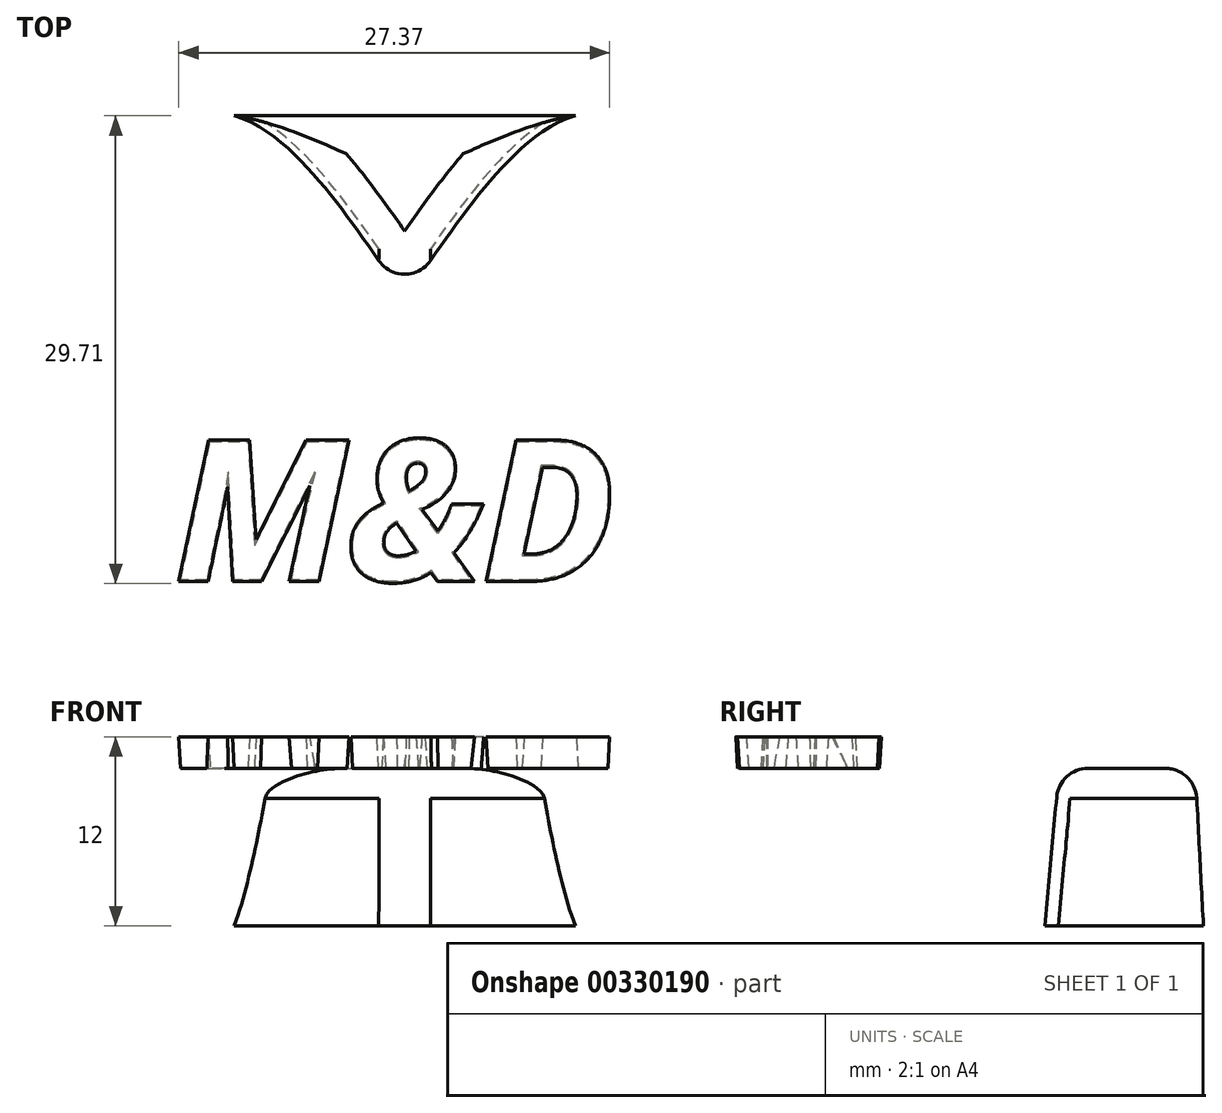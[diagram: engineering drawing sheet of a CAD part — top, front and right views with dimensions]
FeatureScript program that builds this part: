
annotation { "Feature Type Name" : "Feature", "Feature Type Description" : "" }
export const myFeature = defineFeature(function(context is Context, id is Id, definition is map)
    precondition{}
    {
        {
            var Q0;
            Q0=qCreatedBy(makeId("Top.planeOp"),FACE);
            var sketch = newSketch(context, id + "F0", { "sketchPlane" : qUnion([Q0])});
            skLineSegment(sketch, "E0.bottom", {"start": v(-22.5, 22.5) * mm, "end": v(22.5, 22.5) * mm});
            skLineSegment(sketch, "E0.top", {"start": v(-22.5, -22.5) * mm, "end": v(22.5, -22.5) * mm});
            skLineSegment(sketch, "E0.left", {"start": v(-22.5, 22.5) * mm, "end": v(-22.5, -22.5) * mm});
            skLineSegment(sketch, "E0.right", {"start": v(22.5, 22.5) * mm, "end": v(22.5, -22.5) * mm});
            skPoint(sketch, "E0.middle", {"position": v(0, 0) * mm});
            skPoint(sketch, "E1.0.internal.snap0", {"position": v(0, -22.5) * mm});
            skFitSpline(sketch, "E1", {"points": [v(0, -20.95) * mm, v(-22.5, 0) * mm, v(-13.19, 22.5) * mm, v(0, 10.86) * mm], "startDerivative": vector(-82.78, 43.98) * mm, "endDerivative": vector(45.64, -67.78) * mm});
            skFitSpline(sketch, "E2.MirrorCS", {"points": [v(0, -20.95) * mm, v(22.5, 0) * mm, v(13.19, 22.5) * mm, v(0, 10.86) * mm], "startDerivative": vector(82.78, 43.98) * mm, "endDerivative": vector(-45.64, -67.78) * mm});
            skSolve(sketch);
        }
        {
            var Q0;
            {var subQ4=sQuery(id+"F0.wireOp",EDGE,"E1");var subQ6=sQuery(id+"F0.wireOp",EDGE,"E0.bottom");var subQ12=makeQuery(id+"F0.imprint","INTERSECT",VERTEX,{"disambiguationData":[OD(0.0)],"derivedFrom":[subQ6,subQ4]});Q0=makeQuery(id+"F0.imprint","IMPRINT",FACE,{"disambiguationData":[TD([[makeQuery(id+"F0.imprint","IMPRINT",EDGE,{"disambiguationData":[TD([[subQ12,-1.0]])],"derivedFrom":subQ6}),-1.0]])]});}
            extrude(context, id + "F1", {"entities" : qUnion([Q0]), "depth" : 10 * mm, "hasDraft" : true, "draftAngle" : 3 * degree, "draftPullDirection" : true});
        }
        {
            var Q0;
            Q0=makeQuery(id+"F1.opExtrude","CAP_FACE",FACE,{"disambiguationData":[OSD([sQuery(id+"F0.wireOp",EDGE,"E0.bottom"),sQuery(id+"F0.wireOp",EDGE,"E0.left"),sQuery(id+"F0.wireOp",EDGE,"E0.right"),sQuery(id+"F0.wireOp",EDGE,"E1"),sQuery(id+"F0.wireOp",EDGE,"E2.MirrorCS")])],"isStart":false});
            var Q1;
            {var subQ0=sQuery(id+"F0.wireOp",EDGE,"E2.MirrorCS");var subQ1=sQuery(id+"F0.wireOp",EDGE,"E1");Q1=makeQuery(id+"F1.opExtrude","SWEPT_EDGE",EDGE,{"disambiguationData":[OSD([subQ1,subQ0]),TDD([makeQuery(id+"F0.imprint","INTERSECT",VERTEX,{"disambiguationData":[OD(0.0)],"derivedFrom":[subQ1,subQ0]})])]});}
            fillet(context, id + "F2", {"entities" : qUnion([Q0, Q1]), "radius" : 2 * mm, "tangentPropagation" : true, "allowEdgeOverflow" : false});
        }
        {
            var Q0;
            Q0=makeQuery(id+"F1.opExtrude","CAP_FACE",FACE,{"disambiguationData":[OSD([sQuery(id+"F0.wireOp",EDGE,"E0.bottom"),sQuery(id+"F0.wireOp",EDGE,"E0.left"),sQuery(id+"F0.wireOp",EDGE,"E0.right"),sQuery(id+"F0.wireOp",EDGE,"E1"),sQuery(id+"F0.wireOp",EDGE,"E2.MirrorCS")])],"isStart":false});
            var sketch = newSketch(context, id + "F3", { "sketchPlane" : qUnion([Q0])});
            skText(sketch, "E3", { "text": "M&D", "fontName": "OpenSans-BoldItalic.ttf"});
            const initialGuessF3  = {"E3": [-0.01454, -0.00698, 1, 0, 0.00885]};
            skSetInitialGuess(sketch, initialGuessF3);
            skSolve(sketch);
        }
        {
            var Q0;
            Q0 = qSketchRegion(id + "F3", true);
            extrude(context, id + "F4", {"entities" : qUnion([Q0]), "operationType" : NewBodyOperationType.ADD, "depth" : 2 * mm, "hasDraft" : true, "draftAngle" : 3 * degree});
        }
    });
